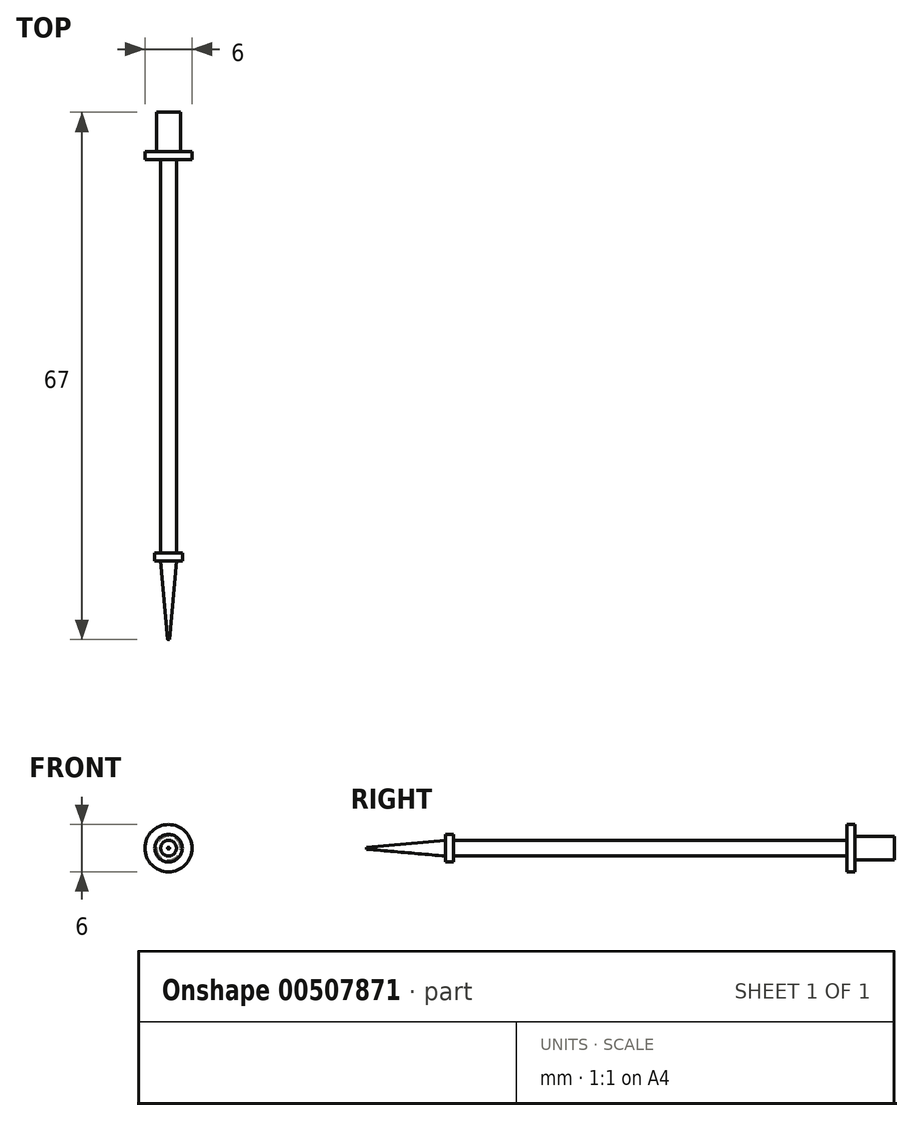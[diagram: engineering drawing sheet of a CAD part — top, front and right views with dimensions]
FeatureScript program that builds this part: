
annotation { "Feature Type Name" : "Feature", "Feature Type Description" : "" }
export const myFeature = defineFeature(function(context is Context, id is Id, definition is map)
    precondition{}
    {
        {
            var Q0;
            Q0=qCreatedBy(makeId("Front.planeOp"),FACE);
            var sketch = newSketch(context, id + "F0", { "sketchPlane" : qUnion([Q0])});
            skCircle(sketch, "E0", {"center": v(0, 0) * mm, "radius": 3 * mm});
            skSolve(sketch);
        }
        {
            var Q0;
            Q0=makeQuery(id+"F0.imprint","IMPRINT",FACE,{"disambiguationData":[TD([[makeQuery(id+"F0.imprint","IMPRINT",EDGE,{"derivedFrom":sQuery(id+"F0.wireOp",EDGE,"E0")}),1.0]])]});
            var Q1;
            Q1=sQuery(id+"F0.wireOp",EDGE,"E0");
            extrude(context, id + "F1", {"entities" : qUnion([Q0]), "surfaceEntities" : qUnion([Q1]), "depth" : 1 * mm, "offsetDistance" : 25 * mm, "symmetric" : true});
        }
        {
            var Q0;
            Q0=makeQuery(id+"F1.opExtrude","CAP_FACE",FACE,{"disambiguationData":[OSD([sQuery(id+"F0.wireOp",EDGE,"E0")])],"isStart":false});
            var sketch = newSketch(context, id + "F2", { "sketchPlane" : qUnion([Q0])});
            skCircle(sketch, "E1", {"center": v(0, 0) * mm, "radius": 1 * mm});
            skSolve(sketch);
        }
        {
            var Q0;
            Q0=makeQuery(id+"F2.imprint","IMPRINT",FACE,{"disambiguationData":[TD([[makeQuery(id+"F2.imprint","IMPRINT",EDGE,{"derivedFrom":sQuery(id+"F2.wireOp",EDGE,"E1")}),1.0]])]});
            extrude(context, id + "F3", {"entities" : qUnion([Q0]), "operationType" : NewBodyOperationType.ADD, "depth" : 50 * mm, "offsetDistance" : 25 * mm});
        }
        {
            var Q0;
            Q0=makeQuery(id+"F1.opExtrude","CAP_FACE",FACE,{"disambiguationData":[OSD([sQuery(id+"F0.wireOp",EDGE,"E0")])],"isStart":true});
            var sketch = newSketch(context, id + "F4", { "sketchPlane" : qUnion([Q0])});
            skCircle(sketch, "E2", {"center": v(0, 0) * mm, "radius": 1.5 * mm});
            skSolve(sketch);
        }
        {
            var Q0;
            Q0=makeQuery(id+"F4.imprint","IMPRINT",FACE,{"disambiguationData":[TD([[makeQuery(id+"F4.imprint","IMPRINT",EDGE,{"derivedFrom":sQuery(id+"F4.wireOp",EDGE,"E2")}),1.0]])]});
            var Q1;
            Q1=sQuery(id+"F4.wireOp",EDGE,"E2");
            extrude(context, id + "F5", {"entities" : qUnion([Q0]), "surfaceEntities" : qUnion([Q1]), "depth" : 5 * mm, "offsetDistance" : 25 * mm});
        }
        {
            var Q0;
            Q0=makeQuery(id+"F3.opExtrude","CAP_FACE",FACE,{"disambiguationData":[OSD([sQuery(id+"F2.wireOp",EDGE,"E1")])],"isStart":false});
            var sketch = newSketch(context, id + "F6", { "sketchPlane" : qUnion([Q0])});
            skCircle(sketch, "E3", {"center": v(0, 0) * mm, "radius": 1.75 * mm});
            skSolve(sketch);
        }
        {
            var Q0;
            Q0=makeQuery(id+"F6.imprint","IMPRINT",FACE,{"disambiguationData":[TD([[makeQuery(id+"F6.imprint","IMPRINT",EDGE,{"derivedFrom":sQuery(id+"F6.wireOp",EDGE,"E3")}),1.0]])]});
            var Q1;
            Q1=makeQuery(id+"F6.imprint","IMPRINT",FACE,{"disambiguationData":[TD([[makeQuery(id+"F6.imprint","IMPRINT",EDGE,{"derivedFrom":makeQuery(id+"F3.opExtrude","CAP_EDGE",EDGE,{"disambiguationData":[OSD([sQuery(id+"F2.wireOp",EDGE,"E1")])],"isStart":false})}),1.0]])]});
            extrude(context, id + "F7", {"entities" : qUnion([Q0, Q1]), "operationType" : NewBodyOperationType.ADD, "depth" : 1 * mm, "offsetDistance" : 25 * mm});
        }
        {
            var Q0;
            Q0=makeQuery(id+"F7.opExtrude","CAP_FACE",FACE,{"disambiguationData":[OSD([sQuery(id+"F6.wireOp",EDGE,"E3")])],"isStart":false});
            var sketch = newSketch(context, id + "F8", { "sketchPlane" : qUnion([Q0])});
            skCircle(sketch, "E4", {"center": v(0, 0) * mm, "radius": 1 * mm});
            skSolve(sketch);
        }
        {
            var Q0;
            Q0=makeQuery(id+"F8.imprint","IMPRINT",FACE,{"disambiguationData":[TD([[makeQuery(id+"F8.imprint","IMPRINT",EDGE,{"derivedFrom":sQuery(id+"F8.wireOp",EDGE,"E4")}),1.0]])]});
            extrude(context, id + "F9", {"entities" : qUnion([Q0]), "operationType" : NewBodyOperationType.ADD, "depth" : 10 * mm, "offsetDistance" : 25 * mm, "hasDraft" : true, "draftAngle" : 5 * degree, "draftPullDirection" : true});
        }
    });
